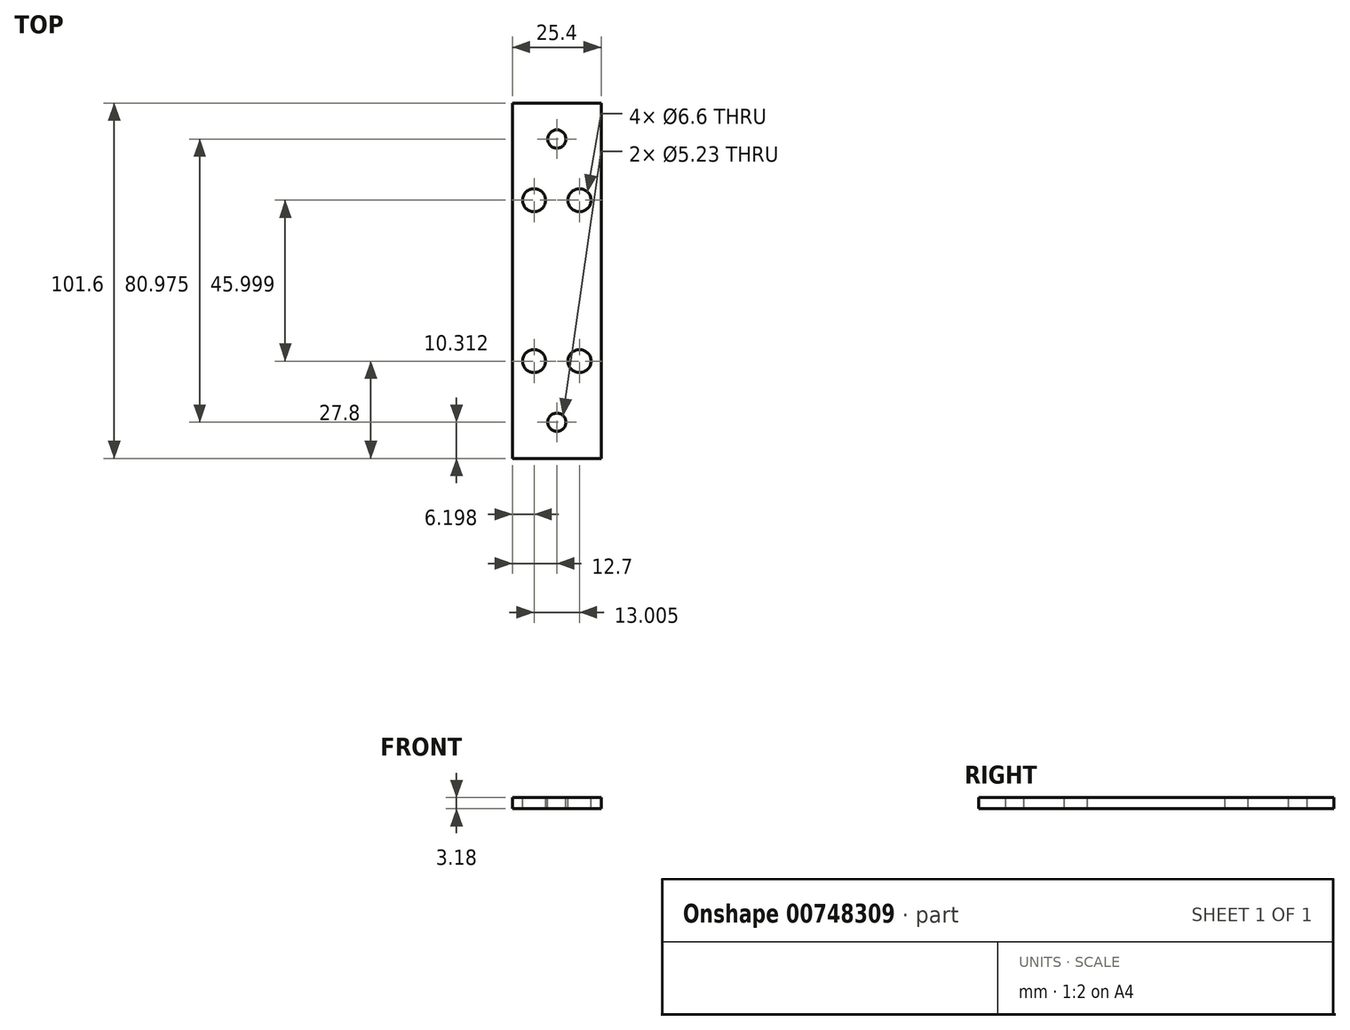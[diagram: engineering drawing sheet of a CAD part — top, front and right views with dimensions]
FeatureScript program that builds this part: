
annotation { "Feature Type Name" : "Feature", "Feature Type Description" : "" }
export const myFeature = defineFeature(function(context is Context, id is Id, definition is map)
    precondition{}
    {
        {
            var Q0;
            Q0=qCreatedBy(makeId("Front.planeOp"),FACE);
            var sketch = newSketch(context, id + "F0", { "sketchPlane" : qUnion([Q0])});
            skLineSegment(sketch, "E0.bottom", {"start": v(12.7, -1.59) * mm, "end": v(-12.7, -1.59) * mm});
            skLineSegment(sketch, "E0.top", {"start": v(12.7, 1.59) * mm, "end": v(-12.7, 1.59) * mm});
            skLineSegment(sketch, "E0.left", {"start": v(12.7, -1.59) * mm, "end": v(12.7, 1.59) * mm});
            skLineSegment(sketch, "E0.right", {"start": v(-12.7, -1.59) * mm, "end": v(-12.7, 1.59) * mm});
            skPoint(sketch, "E0.middle", {"position": v(0, 0) * mm});
            skSolve(sketch);
        }
        {
            var Q0;
            Q0 = qSketchRegion(id + "F0", true);
            extrude(context, id + "F1", {"entities" : qUnion([Q0]), "depth" : 101.6 * mm, "offsetDistance" : 25.4 * mm});
        }
        {
            var Q0;
            Q0=makeQuery(id+"F1.opExtrude","SWEPT_FACE",FACE,{"disambiguationData":[OSD([sQuery(id+"F0.wireOp",EDGE,"E0.top")])]});
            var sketch = newSketch(context, id + "F2", { "sketchPlane" : qUnion([Q0])});
            skLineSegment(sketch, "E1", {"start": v(0, -101.6) * mm, "end": v(0, 0) * mm, "construction": true});
            skLineSegment(sketch, "E2", {"start": v(-12.7, -91.29) * mm, "end": v(12.7, -91.29) * mm, "construction": true});
            skLineSegment(sketch, "E3", {"start": v(-12.7, -10.31) * mm, "end": v(12.7, -10.31) * mm, "construction": true});
            skLineSegment(sketch, "E4", {"start": v(-12.7, -50.8) * mm, "end": v(12.7, -50.8) * mm, "construction": true});
            skCircle(sketch, "E5", {"center": v(0, -91.29) * mm, "radius": 2.62 * mm});
            skCircle(sketch, "E6", {"center": v(0, -10.31) * mm, "radius": 2.62 * mm});
            skLineSegment(sketch, "E7.bottom", {"start": v(6.5, -27.8) * mm, "end": v(-6.5, -27.8) * mm, "construction": true});
            skLineSegment(sketch, "E7.top", {"start": v(6.5, -73.8) * mm, "end": v(-6.5, -73.8) * mm, "construction": true});
            skLineSegment(sketch, "E7.left", {"start": v(6.5, -27.8) * mm, "end": v(6.5, -73.8) * mm, "construction": true});
            skLineSegment(sketch, "E7.right", {"start": v(-6.5, -27.8) * mm, "end": v(-6.5, -73.8) * mm, "construction": true});
            skPoint(sketch, "E7.middle", {"position": v(0, -50.8) * mm});
            skCircle(sketch, "E8", {"center": v(-6.5, -27.8) * mm, "radius": 3.3 * mm});
            skCircle(sketch, "E9", {"center": v(6.5, -27.8) * mm, "radius": 3.3 * mm});
            skCircle(sketch, "E10", {"center": v(6.5, -73.8) * mm, "radius": 3.3 * mm});
            skCircle(sketch, "E11", {"center": v(-6.5, -73.8) * mm, "radius": 3.3 * mm});
            skSolve(sketch);
        }
        {
            var Q0;
            Q0 = qSketchRegion(id + "F2", true);
            extrude(context, id + "F3", {"entities" : qUnion([Q0]), "operationType" : NewBodyOperationType.REMOVE, "endBound" : BoundingType.THROUGH_ALL, "oppositeDirection" : true, "depth" : 25.4 * mm, "offsetDistance" : 25.4 * mm});
        }
    });
